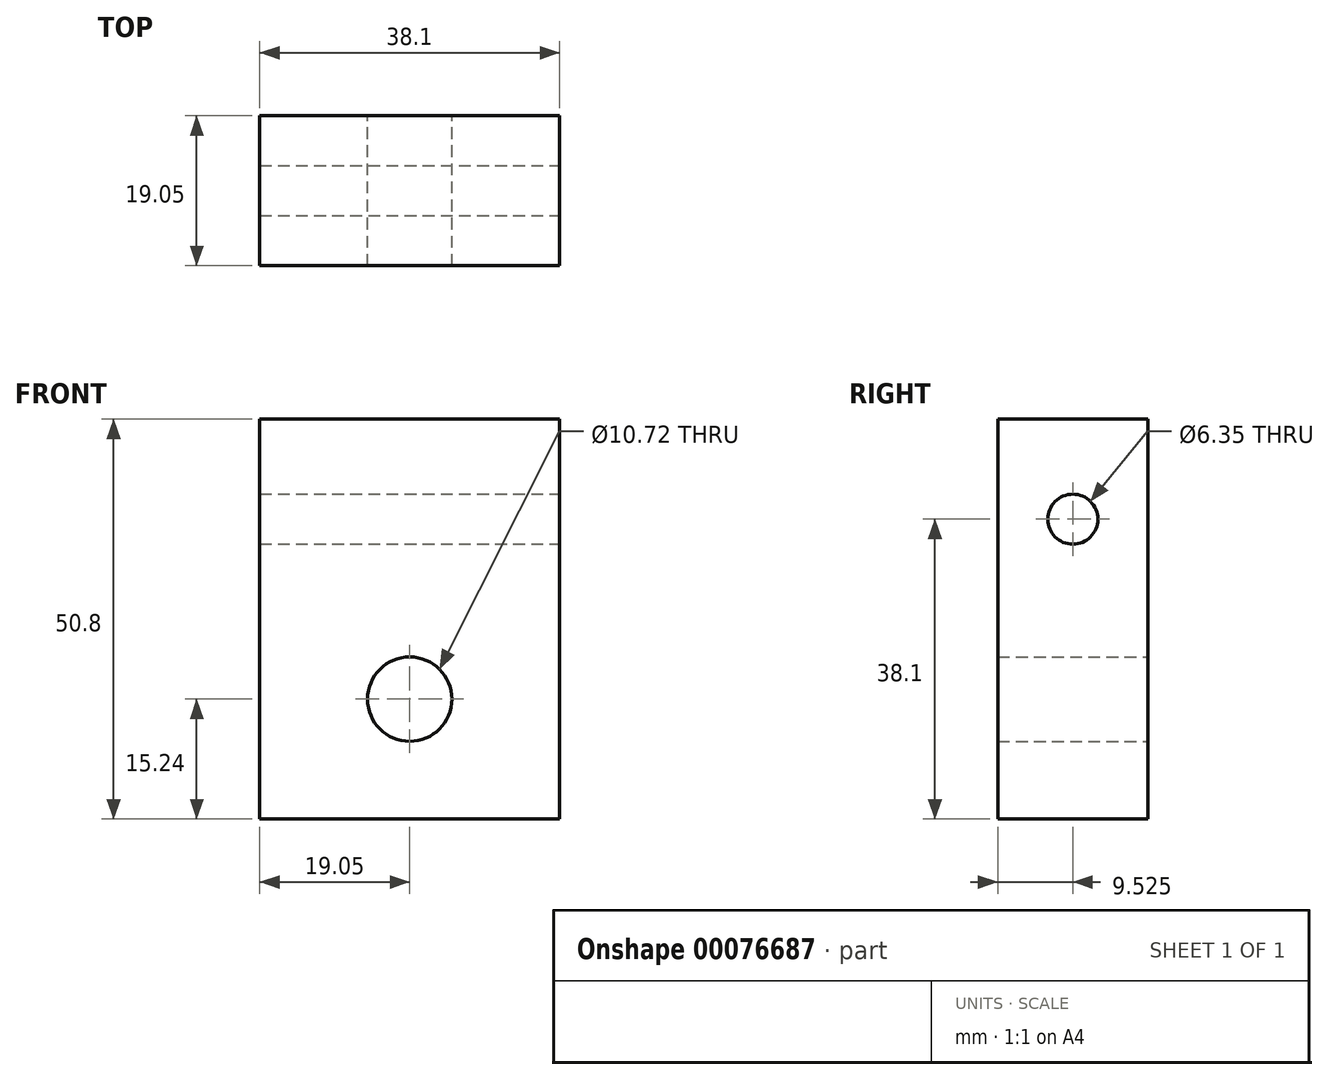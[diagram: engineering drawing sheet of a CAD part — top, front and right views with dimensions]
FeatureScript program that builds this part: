
annotation { "Feature Type Name" : "Feature", "Feature Type Description" : "" }
export const myFeature = defineFeature(function(context is Context, id is Id, definition is map)
    precondition{}
    {
        {
            var Q0;
            Q0=qCreatedBy(makeId("Front.planeOp"),FACE);
            var sketch = newSketch(context, id + "F0", { "sketchPlane" : qUnion([Q0])});
            skLineSegment(sketch, "E0.bottom", {"start": v(0, 0) * mm, "end": v(-38.1, 0) * mm});
            skLineSegment(sketch, "E0.top", {"start": v(0, 50.8) * mm, "end": v(-38.1, 50.8) * mm});
            skLineSegment(sketch, "E0.left", {"start": v(0, 0) * mm, "end": v(0, 50.8) * mm});
            skLineSegment(sketch, "E0.right", {"start": v(-38.1, 0) * mm, "end": v(-38.1, 50.8) * mm});
            skLineSegment(sketch, "E1.0", {"start": v(0, 15.24) * mm, "end": v(-38.1, 15.24) * mm, "construction": true});
            skCircle(sketch, "E2", {"center": v(-19.05, 15.24) * mm, "radius": 5.36 * mm, "construction": true});
            skSolve(sketch);
        }
        {
            var Q0;
            Q0=makeQuery(id+"F0.imprint","IMPRINT",FACE,{"disambiguationData":[TD([[makeQuery(id+"F0.imprint","IMPRINT",EDGE,{"derivedFrom":sQuery(id+"F0.wireOp",EDGE,"E0.bottom")}),-1.0]])]});
            extrude(context, id + "F1", {"entities" : qUnion([Q0]), "depth" : 19.05 * mm});
        }
        {
            var Q0;
            Q0=makeQuery(id+"F1.opExtrude","SWEPT_FACE",FACE,{"disambiguationData":[OSD([sQuery(id+"F0.wireOp",EDGE,"E0.left")])]});
            var sketch = newSketch(context, id + "F2", { "sketchPlane" : qUnion([Q0])});
            skLineSegment(sketch, "E3.0", {"start": v(-19.05, 38.1) * mm, "end": v(0, 38.1) * mm, "construction": true});
            skCircle(sketch, "E4", {"center": v(-9.53, 38.1) * mm, "radius": 3.18 * mm, "construction": true});
            skSolve(sketch);
        }
        {
            var Q0;
            Q0=sQuery(id+"F2.wireOp",VERTEX,"E4.center");
            var Q1;
            Q1=makeQuery(id+"F1.opExtrude","SWEPT_BODY",BODY,{"disambiguationData":[OSD([sQuery(id+"F0.wireOp",EDGE,"E0.bottom"),sQuery(id+"F0.wireOp",EDGE,"E0.top"),sQuery(id+"F0.wireOp",EDGE,"E0.left"),sQuery(id+"F0.wireOp",EDGE,"E0.right")])]});
            hole(context, id + "F3", {"style" : HoleStyle.SIMPLE, "endStyle" : HoleEndStyle.THROUGH, "holeDiameter" : 6.35 * mm, "locations" : qUnion([Q0]), "scope" : qUnion([Q1]), "isTappedThrough" : true});
        }
        {
            var Q0;
            Q0=sQuery(id+"F0.wireOp",VERTEX,"E2.center");
            var Q1;
            Q1=makeQuery(id+"F1.opExtrude","SWEPT_BODY",BODY,{"disambiguationData":[OSD([sQuery(id+"F0.wireOp",EDGE,"E0.bottom"),sQuery(id+"F0.wireOp",EDGE,"E0.top"),sQuery(id+"F0.wireOp",EDGE,"E0.left"),sQuery(id+"F0.wireOp",EDGE,"E0.right")])]});
            hole(context, id + "F4", {"style" : HoleStyle.SIMPLE, "endStyle" : HoleEndStyle.THROUGH, "oppositeDirection" : true, "holeDiameter" : 10.72 * mm, "locations" : qUnion([Q0]), "scope" : qUnion([Q1]), "isTappedThrough" : true});
        }
    });
